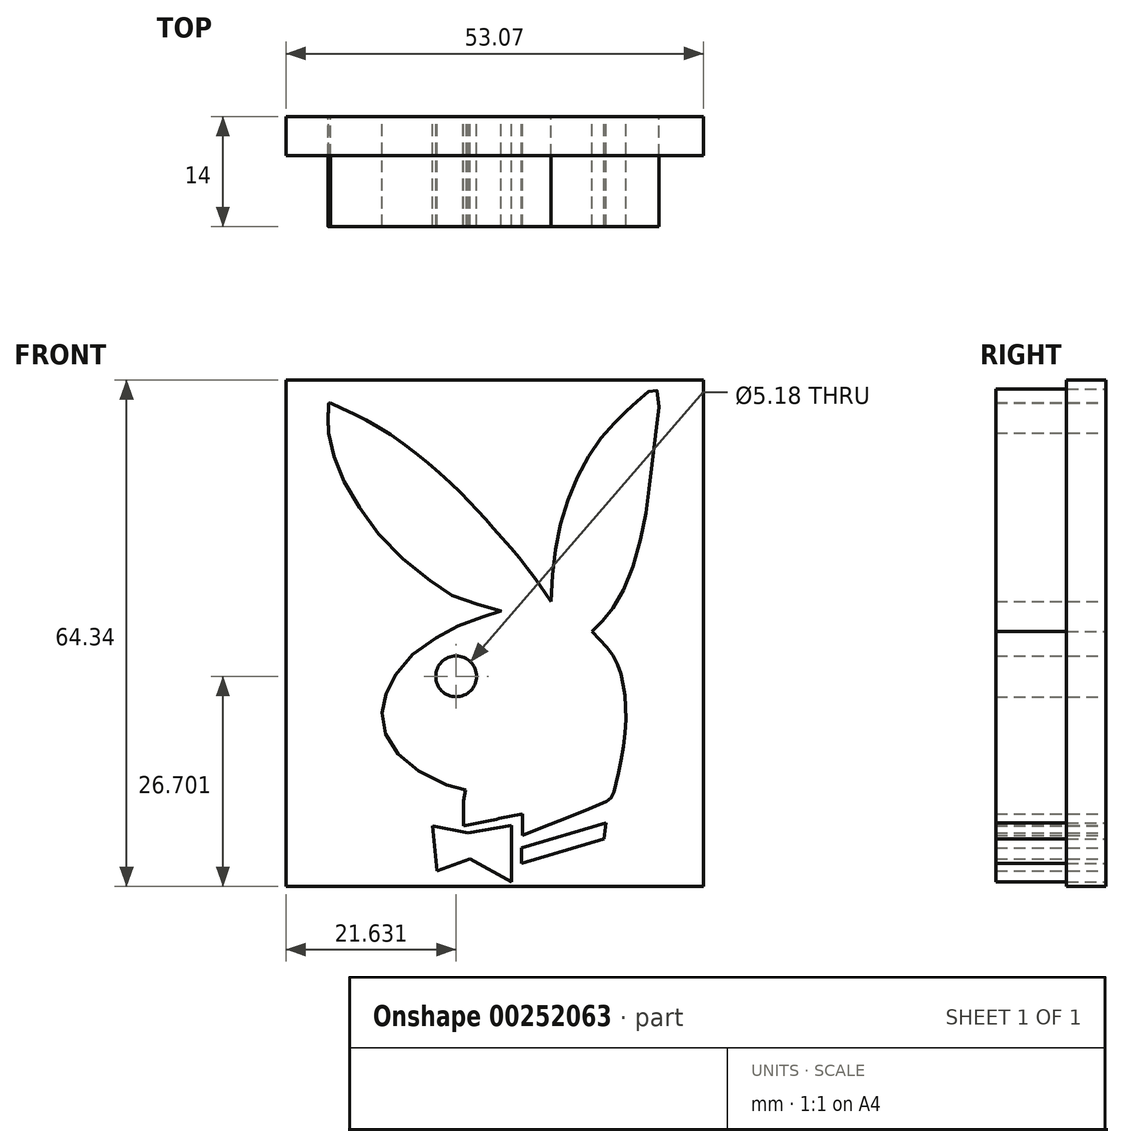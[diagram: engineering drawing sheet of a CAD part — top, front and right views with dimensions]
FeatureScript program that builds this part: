
annotation { "Feature Type Name" : "Feature", "Feature Type Description" : "" }
export const myFeature = defineFeature(function(context is Context, id is Id, definition is map)
    precondition{}
    {
        {
            var Q0;
            Q0=qCreatedBy(makeId("Front.planeOp"),FACE);
            var sketch = newSketch(context, id + "F0", { "sketchPlane" : qUnion([Q0])});
            skFitSpline(sketch, "E0", {"points": [v(-44.65, 57.6) * mm, v(-43.66, 53.77) * mm, v(-41.1, 48.71) * mm, v(-36.55, 42.87) * mm, v(-30.59, 38.08) * mm, v(-26.75, 36.1) * mm, v(-22.72, 35) * mm, v(-25.88, 34.02) * mm, v(-29.56, 32.36) * mm, v(-33.9, 29.51) * mm, v(-36.71, 25.95) * mm, v(-37.62, 23.54) * mm, v(-37.78, 20.82) * mm, v(-36.43, 17.58) * mm, v(-33.04, 14.58) * mm, v(-27.94, 12.36) * mm, v(-27.15, 12.24) * mm, v(-27.39, 11.45) * mm, v(-27.5, 7.7) * mm], "startDerivative": vector(13.5, -67) * mm, "endDerivative": vector(3.44, -79.58) * mm});
            skFitSpline(sketch, "E1", {"points": [v(-27.5, 7.7) * mm, v(-23.87, 8.45) * mm, v(-20, 9.2) * mm], "startDerivative": vector(7.32, 1.54) * mm, "endDerivative": vector(7.7, 1.47) * mm});
            skFitSpline(sketch, "E2", {"points": [v(-20, 9.2) * mm, v(-20, 6.52) * mm], "startDerivative": vector(0, -2.69) * mm, "endDerivative": vector(0, -2.69) * mm});
            skFitSpline(sketch, "E3", {"points": [v(-20, 6.52) * mm, v(-10.24, 10.39) * mm, v(-8.78, 11.26) * mm, v(-8.03, 13.43) * mm, v(-6.96, 19.83) * mm, v(-7.16, 25.36) * mm, v(-8.38, 29.16) * mm, v(-11.19, 32.4) * mm], "startDerivative": vector(54.9, 21.63) * mm, "endDerivative": vector(-22.99, 22.5) * mm});
            skFitSpline(sketch, "E4", {"points": [v(-11.19, 32.4) * mm, v(-9.25, 34.37) * mm, v(-6.72, 38.68) * mm, v(-4.35, 47.37) * mm, v(-3.44, 54.68) * mm, v(-2.78, 62.74) * mm, v(-3.37, 63.17) * mm, v(-5.23, 61.87) * mm, v(-7, 60.23) * mm, v(-9.96, 57.03) * mm, v(-13.2, 51.68) * mm, v(-15.55, 44.35) * mm, v(-16.4, 36.22) * mm], "startDerivative": vector(31.9, 29.53) * mm, "endDerivative": vector(-4.9, -78.94) * mm});
            skFitSpline(sketch, "E5", {"points": [v(-16.4, 36.22) * mm, v(-19.07, 40.07) * mm, v(-23.91, 45.76) * mm, v(-28.7, 50.83) * mm, v(-37.02, 57.55) * mm, v(-44.4, 61.45) * mm], "startDerivative": vector(-15.07, 23.17) * mm, "endDerivative": vector(-34.24, 15.84) * mm});
            skFitSpline(sketch, "E6", {"points": [v(-44.4, 61.45) * mm, v(-44.54, 61.45) * mm, v(-44.62, 61.25) * mm, v(-44.67, 58.53) * mm, v(-44.65, 57.6) * mm], "startDerivative": vector(-1.43, 0.2) * mm, "endDerivative": vector(0.07, -2.5) * mm});
            skCircle(sketch, "E7", {"center": v(-28.43, 26.7) * mm, "radius": 2.59 * mm});
            skLineSegment(sketch, "E8", {"start": v(-31.43, 7.73) * mm, "end": v(-30.87, 1.98) * mm});
            skLineSegment(sketch, "E9", {"start": v(-30.87, 1.98) * mm, "end": v(-26.68, 3.49) * mm});
            skLineSegment(sketch, "E10", {"start": v(-26.68, 3.49) * mm, "end": v(-21.38, 0.58) * mm});
            skLineSegment(sketch, "E11", {"start": v(-21.38, 0.58) * mm, "end": v(-21.38, 7.79) * mm});
            skLineSegment(sketch, "E12", {"start": v(-21.38, 7.79) * mm, "end": v(-26.9, 6.78) * mm});
            skLineSegment(sketch, "E13", {"start": v(-26.9, 6.78) * mm, "end": v(-31.43, 7.73) * mm});
            skLineSegment(sketch, "E14", {"start": v(-20.15, 4.94) * mm, "end": v(-20.15, 2.93) * mm});
            skLineSegment(sketch, "E15", {"start": v(-20.15, 2.93) * mm, "end": v(-9.64, 6.06) * mm});
            skLineSegment(sketch, "E16", {"start": v(-9.64, 6.06) * mm, "end": v(-9.38, 8.06) * mm});
            skLineSegment(sketch, "E17", {"start": v(-9.38, 8.06) * mm, "end": v(-20.15, 4.94) * mm});
            skSolve(sketch);
        }
        {
            var Q0;
            Q0=makeQuery(id+"F0.imprint","IMPRINT",FACE,{"disambiguationData":[TD([[makeQuery(id+"F0.imprint","IMPRINT",EDGE,{"derivedFrom":sQuery(id+"F0.wireOp",EDGE,"E0")}),-1.0]])]});
            var Q1;
            Q1=makeQuery(id+"F0.imprint","IMPRINT",FACE,{"disambiguationData":[TD([[makeQuery(id+"F0.imprint","IMPRINT",EDGE,{"derivedFrom":sQuery(id+"F0.wireOp",EDGE,"E0")}),1.0]])]});
            var Q2;
            Q2=makeQuery(id+"F0.imprint","IMPRINT",FACE,{"disambiguationData":[TD([[makeQuery(id+"F0.imprint","IMPRINT",EDGE,{"derivedFrom":sQuery(id+"F0.wireOp",EDGE,"E8")}),1.0]])]});
            var Q3;
            Q3=makeQuery(id+"F0.imprint","IMPRINT",FACE,{"disambiguationData":[TD([[makeQuery(id+"F0.imprint","IMPRINT",EDGE,{"derivedFrom":sQuery(id+"F0.wireOp",EDGE,"E14")}),1.0]])]});
            var Q4;
            Q4 = qSketchRegion(id + "F2", true);
            var Q5;
            Q5 = qConstructionFilter(qBodyType(qCreatedBy(id + "F0" ,EDGE), BodyType.WIRE), ConstructionObject.NO);
            extrude(context, id + "F1", {"entities" : qUnion([Q0, Q1, Q2, Q3, Q4]), "surfaceEntities" : qUnion([Q5]), "depth" : 14 * mm, "offsetDistance" : 25 * mm});
        }
        {
            var Q0;
            Q0=qCreatedBy(makeId("Front.planeOp"),FACE);
            var sketch = newSketch(context, id + "F2", { "sketchPlane" : qUnion([Q0])});
            skLineSegment(sketch, "E18.bottom", {"start": v(-50.06, 64.34) * mm, "end": v(3.01, 64.34) * mm});
            skLineSegment(sketch, "E18.top", {"start": v(-50.06, 0) * mm, "end": v(3.01, 0) * mm});
            skLineSegment(sketch, "E18.left", {"start": v(-50.06, 64.34) * mm, "end": v(-50.06, 0) * mm});
            skLineSegment(sketch, "E18.right", {"start": v(3.01, 64.34) * mm, "end": v(3.01, 0) * mm});
            skSolve(sketch);
        }
        {
            var Q0;
            Q0=makeQuery(id+"F2.imprint","IMPRINT",FACE,{"disambiguationData":[TD([[makeQuery(id+"F2.imprint","IMPRINT",EDGE,{"derivedFrom":sQuery(id+"F2.wireOp",EDGE,"E18.bottom")}),-1.0]])]});
            extrude(context, id + "F3", {"entities" : qUnion([Q0]), "depth" : 5 * mm, "offsetDistance" : 25 * mm});
        }
    });
